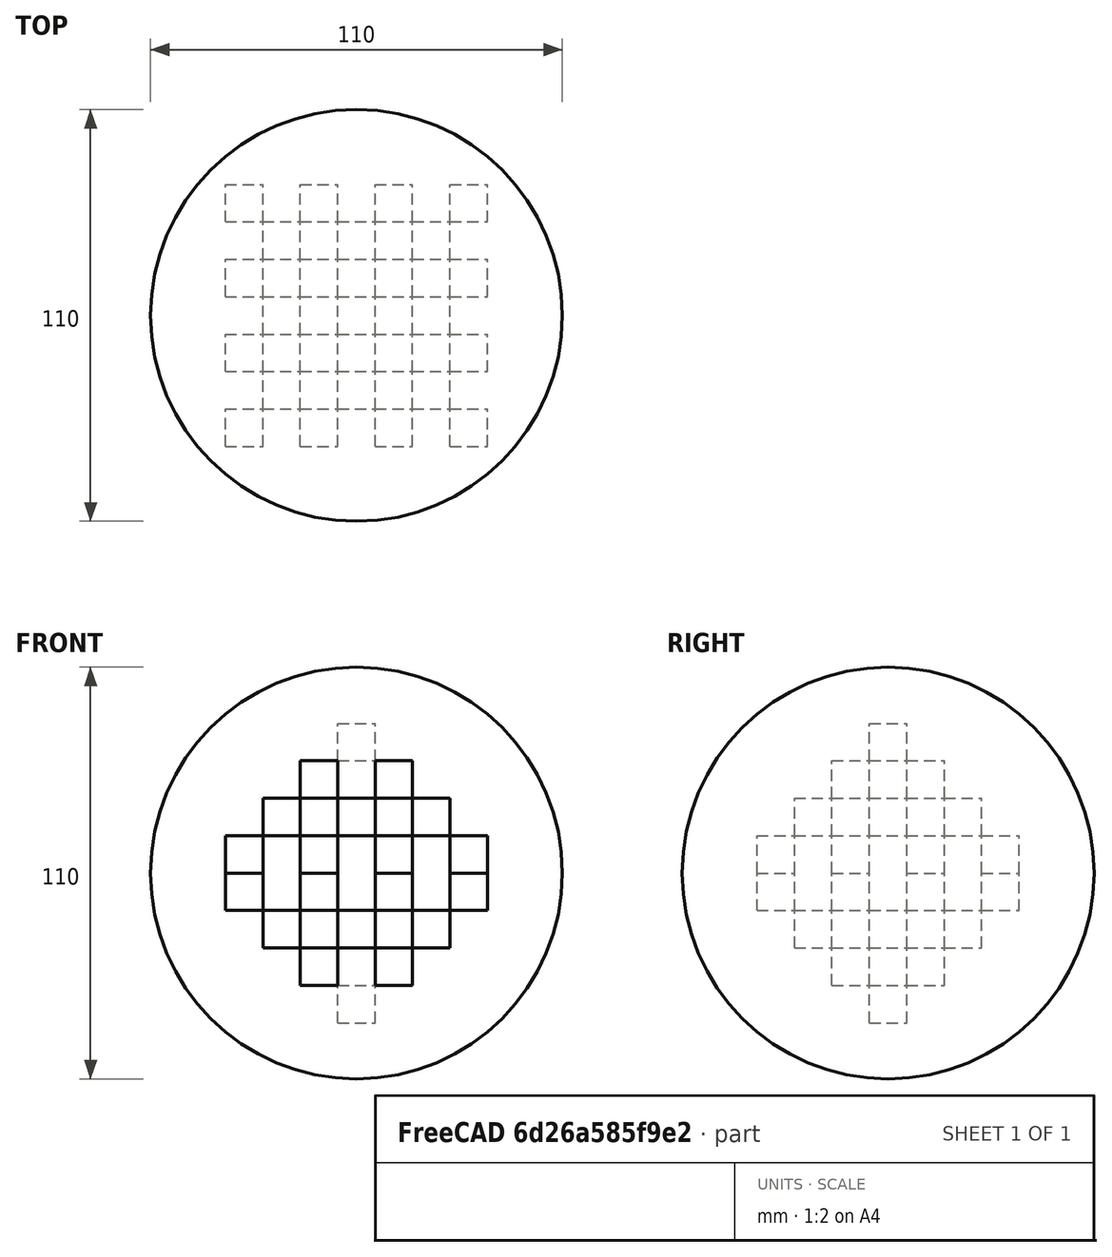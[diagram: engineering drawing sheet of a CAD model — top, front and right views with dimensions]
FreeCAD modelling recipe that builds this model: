
FCSTD DOCUMENT  (FreeCAD 1.0R39319 (Git))
Label: tacevedo_repte1
License: All rights reserved
LicenseURL: https://en.wikipedia.org/wiki/All_rights_reserved
objects: Part::Box×8, Part::FeaturePython×6, Part::MultiFuse×2, Part::Sphere×1
note: 11 computed .brp shape members not serialized (recipe doc carries the construction recipe); baked Part::Feature solids carry a one-line shape summary decoded from their .brp

FEATURE [Part::Box] Box  label="Cub"
  AttacherType = Attacher::AttachEngine3D
  Height = 10
  Length = 10
  Width = 10
FEATURE [Part::FeaturePython] Array  label="pis 1"  # Draft array (typed FeaturePython)
  AlwaysSyncPlacement = false
  Angle = 360
  ArrayType = 0
  Axis = (0,0,1)
  Base = -> Box
  Center = (0,0,0)
  Count = 16
  ExpandArray = false
  Fuse = false
  IntervalAxis = (0,0,0)
  IntervalX = (20,0,0)
  IntervalY = (0,20,0)
  IntervalZ = (0,0,100)
  NumberCircles = 3
  NumberPolar = 5
  NumberX = 4
  NumberY = 4
  NumberZ = 1
  PlacementList = 16 placements: [(0,0,0),(0,20,0),(0,40,0),(0,60,0),(20,0,0),(20,20,0),(20,40,0),(20,60,0),(40,0,0),(40,20,0),(40,40,0),(40,60,0),(60,0,0),(60,20,0),(60,40,0),(60,60,0)]
  RadialDistance = 50
  ScaleList = (16) [(1,1,1),(1,1,1),(1,1,1),(1,1,1),(1,1,1),(1,1,1),(1,1,1),(1,1,1),(1,1,1),(1,1,1),(1,1,1),(1,1,1),(1,1,1),(1,1,1),(1,1,1),(1,1,1)]
  Symmetry = 1
  TangentialDistance = 25
FEATURE [Part::Box] Box001  label="Cub001"
  AttacherType = Attacher::AttachEngine3D
  Height = 10
  Length = 10
  Width = 10
FEATURE [Part::FeaturePython] Array001  label="pis 2"  # Draft array (typed FeaturePython)
  AlwaysSyncPlacement = false
  Angle = 360
  ArrayType = 0
  Axis = (0,0,1)
  Base = -> Box001
  Center = (0,0,0)
  Count = 9
  ExpandArray = false
  Fuse = false
  IntervalAxis = (0,0,0)
  IntervalX = (20,0,0)
  IntervalY = (0,20,0)
  IntervalZ = (0,0,10)
  NumberCircles = 3
  NumberPolar = 5
  NumberX = 3
  NumberY = 3
  NumberZ = 1
  Placement = pos=(10,10,10) rot=(0,0,1;0rad)
  PlacementList = 9 placements: [(0,0,0),(0,20,0),(0,40,0),(20,0,0),(20,20,0),(20,40,0),(40,0,0),(40,20,0),(40,40,0)]
  RadialDistance = 50
  ScaleList = (9) [(1,1,1),(1,1,1),(1,1,1),(1,1,1),(1,1,1),(1,1,1),(1,1,1),(1,1,1),(1,1,1)]
  Symmetry = 1
  TangentialDistance = 25
FEATURE [Part::Box] Box002  label="Cub002"
  AttacherType = Attacher::AttachEngine3D
  Height = 10
  Length = 10
  Width = 10
FEATURE [Part::FeaturePython] Array002  label="pis 3"  # Draft array (typed FeaturePython)
  AlwaysSyncPlacement = false
  Angle = 360
  ArrayType = 0
  Axis = (0,0,1)
  Base = -> Box002
  Center = (0,0,0)
  Count = 4
  ExpandArray = false
  Fuse = false
  IntervalAxis = (0,0,0)
  IntervalX = (20,0,0)
  IntervalY = (0,20,0)
  IntervalZ = (0,0,0)
  NumberCircles = 3
  NumberPolar = 5
  NumberX = 2
  NumberY = 2
  NumberZ = 1
  Placement = pos=(20,20,20) rot=(0,0,1;0rad)
  PlacementList = 4 placements: [(0,0,0),(0,20,0),(20,0,0),(20,20,0)]
  RadialDistance = 50
  ScaleList = (4) [(1,1,1),(1,1,1),(1,1,1),(1,1,1)]
  Symmetry = 1
  TangentialDistance = 25
FEATURE [Part::Box] Box003  label="psi 4"
  AttacherType = Attacher::AttachEngine3D
  Height = 10
  Length = 10
  Placement = pos=(30,30,30) rot=(0,0,1;0rad)
  Width = 10
FEATURE [Part::MultiFuse] Fusion
  Refine = true
  Shapes = -> [Array,Array001,Array002,Box003]
FEATURE [Part::Box] Box004  label="Cub003"
  AttacherType = Attacher::AttachEngine3D
  Height = 10
  Length = 10
  Width = 10
FEATURE [Part::FeaturePython] Array003  label="pis 004"  # Draft array (typed FeaturePython)
  AlwaysSyncPlacement = false
  Angle = 360
  ArrayType = 0
  Axis = (0,0,1)
  Base = -> Box004
  Center = (0,0,0)
  Count = 16
  ExpandArray = false
  Fuse = false
  IntervalAxis = (0,0,0)
  IntervalX = (20,0,0)
  IntervalY = (0,20,0)
  IntervalZ = (0,0,100)
  NumberCircles = 3
  NumberPolar = 5
  NumberX = 4
  NumberY = 4
  NumberZ = 1
  Placement = pos=(0,0,30) rot=(0,0,1;0rad)
  PlacementList = 16 placements: [(0,0,0),(0,20,0),(0,40,0),(0,60,0),(20,0,0),(20,20,0),(20,40,0),(20,60,0),(40,0,0),(40,20,0),(40,40,0),(40,60,0),(60,0,0),(60,20,0),(60,40,0),(60,60,0)]
  RadialDistance = 50
  ScaleList = (16) [(1,1,1),(1,1,1),(1,1,1),(1,1,1),(1,1,1),(1,1,1),(1,1,1),(1,1,1),(1,1,1),(1,1,1),(1,1,1),(1,1,1),(1,1,1),(1,1,1),(1,1,1),(1,1,1)]
  Symmetry = 1
  TangentialDistance = 25
FEATURE [Part::Box] Box005  label="Cub004"
  AttacherType = Attacher::AttachEngine3D
  Height = 10
  Length = 10
  Width = 10
FEATURE [Part::FeaturePython] Array004  label="pis 005"  # Draft array (typed FeaturePython)
  AlwaysSyncPlacement = false
  Angle = 360
  ArrayType = 0
  Axis = (0,0,1)
  Base = -> Box005
  Center = (0,0,0)
  Count = 9
  ExpandArray = false
  Fuse = false
  IntervalAxis = (0,0,0)
  IntervalX = (20,0,0)
  IntervalY = (0,20,0)
  IntervalZ = (0,0,10)
  NumberCircles = 3
  NumberPolar = 5
  NumberX = 3
  NumberY = 3
  NumberZ = 1
  Placement = pos=(10,10,20) rot=(0,0,1;0rad)
  PlacementList = 9 placements: [(0,0,0),(0,20,0),(0,40,0),(20,0,0),(20,20,0),(20,40,0),(40,0,0),(40,20,0),(40,40,0)]
  RadialDistance = 50
  ScaleList = (9) [(1,1,1),(1,1,1),(1,1,1),(1,1,1),(1,1,1),(1,1,1),(1,1,1),(1,1,1),(1,1,1)]
  Symmetry = 1
  TangentialDistance = 25
FEATURE [Part::Box] Box006  label="Cub005"
  AttacherType = Attacher::AttachEngine3D
  Height = 10
  Length = 10
  Width = 10
FEATURE [Part::FeaturePython] Array005  label="pis 006"  # Draft array (typed FeaturePython)
  AlwaysSyncPlacement = false
  Angle = 360
  ArrayType = 0
  Axis = (0,0,1)
  Base = -> Box006
  Center = (0,0,0)
  Count = 4
  ExpandArray = false
  Fuse = false
  IntervalAxis = (0,0,0)
  IntervalX = (20,0,0)
  IntervalY = (0,20,0)
  IntervalZ = (0,0,0)
  NumberCircles = 3
  NumberPolar = 5
  NumberX = 2
  NumberY = 2
  NumberZ = 1
  Placement = pos=(20,20,10) rot=(0,0,1;0rad)
  PlacementList = 4 placements: [(0,0,0),(0,20,0),(20,0,0),(20,20,0)]
  RadialDistance = 50
  ScaleList = (4) [(1,1,1),(1,1,1),(1,1,1),(1,1,1)]
  Symmetry = 1
  TangentialDistance = 25
FEATURE [Part::Box] Box007  label="psi 005"
  AttacherType = Attacher::AttachEngine3D
  Height = 10
  Length = 10
  Placement = pos=(30,30,0) rot=(0,0,1;0rad)
  Width = 10
FEATURE [Part::MultiFuse] Fusion001
  Placement = pos=(0,0,-40) rot=(0,0,1;0rad)
  Refine = true
  Shapes = -> [Array003,Array004,Array005,Box007]
FEATURE [Part::Sphere] Sphere  label="Esfera"
  Angle1 = -90
  Angle2 = 90
  Angle3 = 360
  AttacherType = Attacher::AttachEngine3D
  Placement = pos=(35,35,0) rot=(0,0,1;0rad)
  Radius = 55
